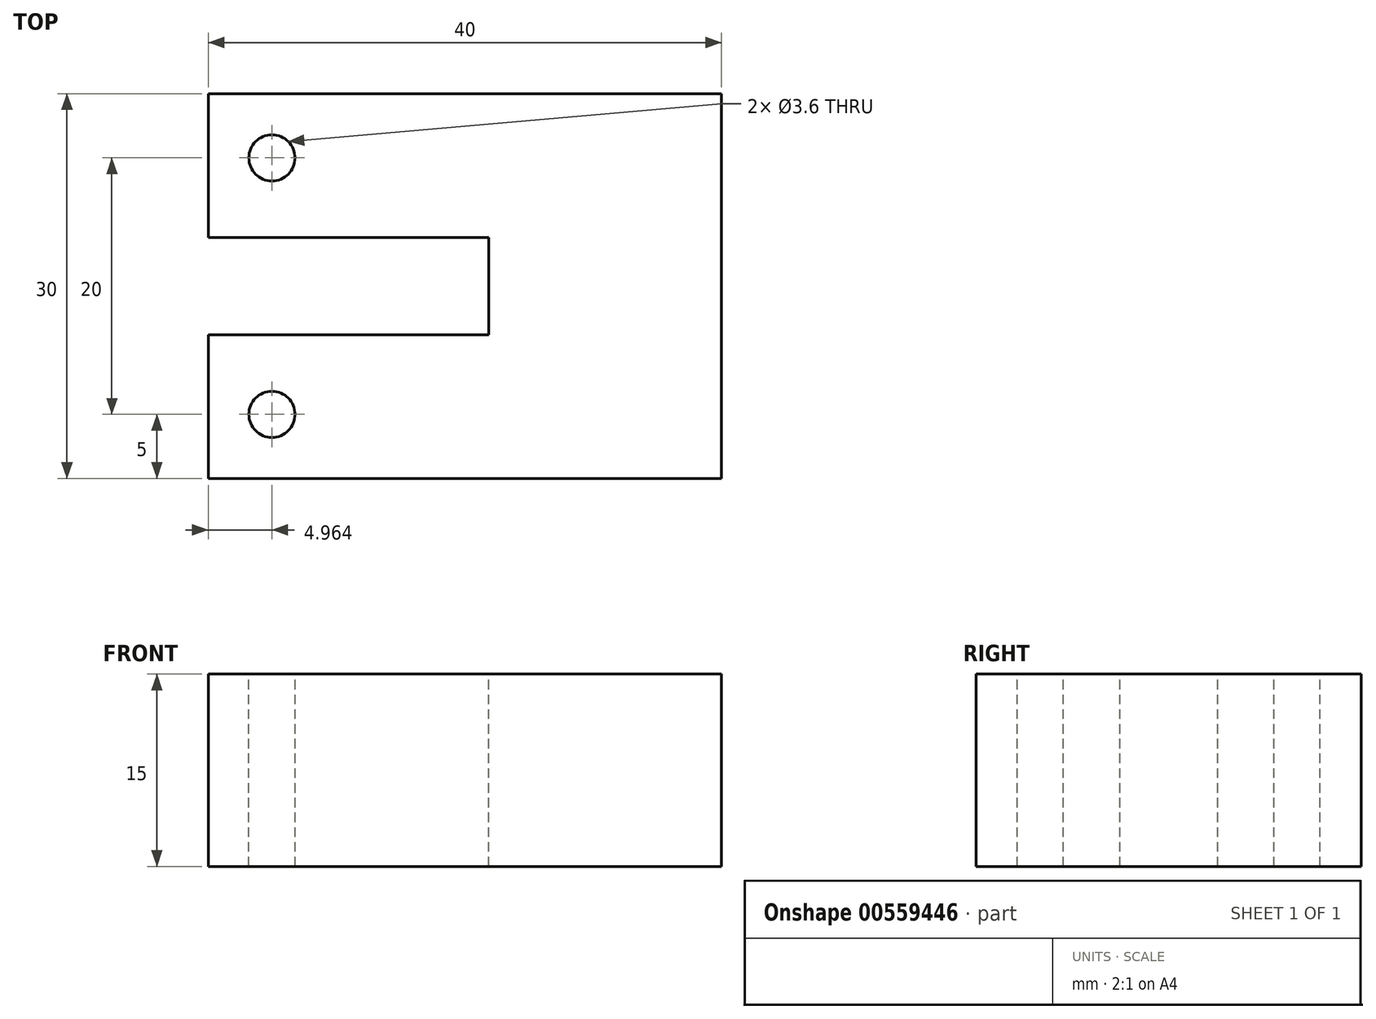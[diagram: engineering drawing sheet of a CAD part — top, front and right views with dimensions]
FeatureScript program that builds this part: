
annotation { "Feature Type Name" : "Feature", "Feature Type Description" : "" }
export const myFeature = defineFeature(function(context is Context, id is Id, definition is map)
    precondition{}
    {
        {
            var Q0;
            Q0=qCreatedBy(makeId("Top.planeOp"),FACE);
            var sketch = newSketch(context, id + "F0", { "sketchPlane" : qUnion([Q0])});
            skLineSegment(sketch, "E0.bottom", {"start": v(20, 15) * mm, "end": v(-20, 15) * mm});
            skLineSegment(sketch, "E0.top", {"start": v(20, -15) * mm, "end": v(-20, -15) * mm});
            skLineSegment(sketch, "E0.left", {"start": v(20, 15) * mm, "end": v(20, -15) * mm});
            skLineSegment(sketch, "E0.right", {"start": v(-20, 15) * mm, "end": v(-20, -15) * mm});
            skPoint(sketch, "E0.middle", {"position": v(0, 0) * mm});
            skSolve(sketch);
        }
        {
            var Q0;
            Q0=qSketchRegion(id+"F0",true);
            extrude(context, id + "F1", {"entities" : qUnion([Q0]), "endBound" : BoundingType.SYMMETRIC, "depth" : 15 * mm, "offsetDistance" : 25 * mm});
        }
        {
            var Q0;
            Q0=makeQuery(id+"F1.opExtrude","CAP_FACE",FACE,{"disambiguationData":[OSD([sQuery(id+"F0.wireOp",EDGE,"E0.bottom"),sQuery(id+"F0.wireOp",EDGE,"E0.top"),sQuery(id+"F0.wireOp",EDGE,"E0.left"),sQuery(id+"F0.wireOp",EDGE,"E0.right")])],"isStart":false});
            var sketch = newSketch(context, id + "F2", { "sketchPlane" : qUnion([Q0])});
            skLineSegment(sketch, "E1.bottom", {"start": v(-20, 3.8) * mm, "end": v(1.86, 3.8) * mm});
            skLineSegment(sketch, "E1.top", {"start": v(-20, -3.8) * mm, "end": v(1.86, -3.8) * mm});
            skLineSegment(sketch, "E1.left", {"start": v(-20, 3.8) * mm, "end": v(-20, -3.8) * mm});
            skLineSegment(sketch, "E1.right", {"start": v(1.86, 3.8) * mm, "end": v(1.86, -3.8) * mm});
            skPoint(sketch, "E1.middle", {"position": v(-9.07, 0) * mm});
            skSolve(sketch);
        }
        {
            var Q0;
            Q0=qSketchRegion(id+"F2",true);
            extrude(context, id + "F3", {"entities" : qUnion([Q0]), "operationType" : NewBodyOperationType.REMOVE, "oppositeDirection" : true, "depth" : 25 * mm, "offsetDistance" : 25 * mm});
        }
        {
            var Q0;
            Q0=makeQuery(id+"F1.opExtrude","CAP_FACE",FACE,{"disambiguationData":[OSD([sQuery(id+"F0.wireOp",EDGE,"E0.bottom"),sQuery(id+"F0.wireOp",EDGE,"E0.top"),sQuery(id+"F0.wireOp",EDGE,"E0.left"),sQuery(id+"F0.wireOp",EDGE,"E0.right")])],"isStart":false});
            var sketch = newSketch(context, id + "F4", { "sketchPlane" : qUnion([Q0])});
            skCircle(sketch, "E2", {"center": v(-15.04, -10) * mm, "radius": 1.8 * mm});
            skCircle(sketch, "E3", {"center": v(-15.04, 10) * mm, "radius": 1.8 * mm});
            skSolve(sketch);
        }
        {
            var Q0;
            Q0=qSketchRegion(id+"F4",true);
            extrude(context, id + "F5", {"entities" : qUnion([Q0]), "operationType" : NewBodyOperationType.REMOVE, "oppositeDirection" : true, "depth" : 20 * mm, "offsetDistance" : 25 * mm});
        }
    });
